# Revit family: Gira_026865
name_source: partatom
category: Electrical Fixtures
revit_build: Autodesk Revit 2017 (Build: 20160225_1515(x64)
units: mm (PartAtom-declared; Revit-internal decimal feet)

## family parameters
Cut with Voids When Loaded = No
Host = Face
Maintain Annotation Orientation = Yes
Part Type = Normal
Room Calculation Point = No
Round Connector Dimension = Use Diameter
Shared = No

## types (1)
- Blank cov.pl. Gira TX_44 (WP FM) c.alum.
    Assembly arrangement = Central cover plate
    Available = No
    BIM (1) = https://media.stage.bim.site und Tasten.rfa?public/gira/36a6b08/Türstation_Schalten und Tasten.rfa
    Category = Insert/cover for communication technology
    Colour = Aluminium
    Data sheet (1) = https://katalog.gira.de
    Default Elevation = 1219 mm
    Description = Bl.cov.pl. TX_44 CAl,Blank cover plate,,colour aluminium,Notes :,- Wall plugs must be used for the frames when using 1-gang frames.
    GTIN = 4010337268659
    HAN = 026865
    Halogen free = No
    HeinzeBIM = https://bimportal.heinze.de
    Imprintable label = Without indication field
    Luster terminal = No
    Manufacturer = Gira
    Manufacturer URL = https://www.gira.de
    Material = Other
    Material quality = Other
    Mounting method = Flush mounted (plaster)
    Name = Blank cov.pl. Gira TX_44 (WP FM) c.alum.
    Suitable for degree of protection (IP) = IP44
    Support ring = No
    Surface finishing = Not applicable
    Surface protection = Other
    Transparent = No
    Type of fastening = Mounting with screw
    URL = http://katalog.gira.de
    Utilization = Blind cap
    With dust cover = No
    With hinged lid = No
    With imprint = No
    With strain relief = No

## geometry (parser evidence)
native form markers: Sweep x3
no freeform markers — native parametric forms only
